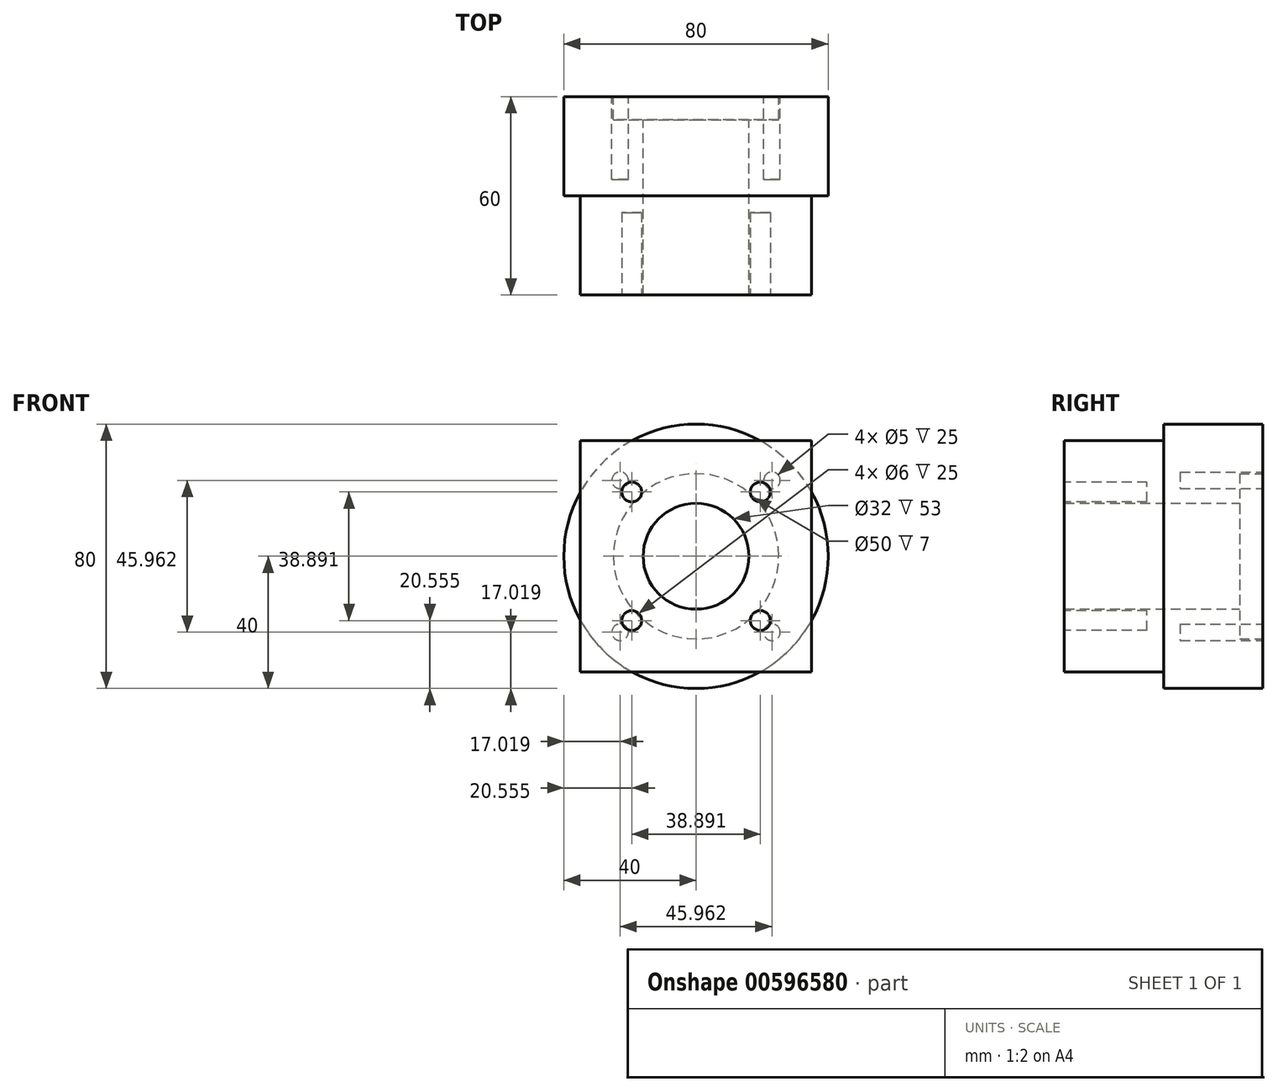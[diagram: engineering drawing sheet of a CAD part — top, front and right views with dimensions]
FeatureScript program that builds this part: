
annotation { "Feature Type Name" : "Feature", "Feature Type Description" : "" }
export const myFeature = defineFeature(function(context is Context, id is Id, definition is map)
    precondition{}
    {
        {
            var Q0;
            Q0=qCreatedBy(makeId("Front.planeOp"),FACE);
            var sketch = newSketch(context, id + "F0", { "sketchPlane" : qUnion([Q0])});
            skCircle(sketch, "E0", {"center": v(0, 0) * mm, "radius": 40 * mm});
            skSolve(sketch);
        }
        {
            var Q0;
            Q0=qSketchRegion(id+"F0",true);
            extrude(context, id + "F1", {"entities" : qUnion([Q0]), "depth" : 30 * mm, "offsetDistance" : 25 * mm});
        }
        {
            var Q0;
            Q0=makeQuery(id+"F1.opExtrude","CAP_FACE",FACE,{"disambiguationData":[OSD([sQuery(id+"F0.wireOp",EDGE,"E0")])],"isStart":false});
            var sketch = newSketch(context, id + "F2", { "sketchPlane" : qUnion([Q0])});
            skLineSegment(sketch, "E1.bottom", {"start": v(-35, -35) * mm, "end": v(35, -35) * mm});
            skLineSegment(sketch, "E1.top", {"start": v(-35, 35) * mm, "end": v(35, 35) * mm});
            skLineSegment(sketch, "E1.left", {"start": v(-35, -35) * mm, "end": v(-35, 35) * mm});
            skLineSegment(sketch, "E1.right", {"start": v(35, -35) * mm, "end": v(35, 35) * mm});
            skSolve(sketch);
        }
        {
            var Q0;
            Q0=qSketchRegion(id+"F2",true);
            extrude(context, id + "F3", {"entities" : qUnion([Q0]), "operationType" : NewBodyOperationType.ADD, "depth" : 30 * mm, "offsetDistance" : 25 * mm});
        }
        {
            var Q0;
            Q0=makeQuery(id+"F1.opExtrude","CAP_FACE",FACE,{"disambiguationData":[OSD([sQuery(id+"F0.wireOp",EDGE,"E0")])],"isStart":true});
            var sketch = newSketch(context, id + "F4", { "sketchPlane" : qUnion([Q0])});
            skCircle(sketch, "E2", {"center": v(0, 0) * mm, "radius": 16 * mm});
            skSolve(sketch);
        }
        {
            var Q0;
            Q0=makeQuery(id+"F4.imprint","IMPRINT",FACE,{"disambiguationData":[TD([[makeQuery(id+"F4.imprint","IMPRINT",EDGE,{"derivedFrom":sQuery(id+"F4.wireOp",EDGE,"E2")}),1.0]])]});
            extrude(context, id + "F5", {"entities" : qUnion([Q0]), "operationType" : NewBodyOperationType.REMOVE, "endBound" : BoundingType.THROUGH_ALL, "oppositeDirection" : true, "depth" : 25 * mm, "offsetDistance" : 25 * mm});
        }
        {
            var Q0;
            Q0=makeQuery(id+"F1.opExtrude","CAP_FACE",FACE,{"disambiguationData":[OSD([sQuery(id+"F0.wireOp",EDGE,"E0")])],"isStart":true});
            var sketch = newSketch(context, id + "F6", { "sketchPlane" : qUnion([Q0])});
            skCircle(sketch, "E3", {"center": v(0, 0) * mm, "radius": 25 * mm});
            skSolve(sketch);
        }
        {
            var Q0;
            Q0=makeQuery(id+"F6.imprint","IMPRINT",FACE,{"disambiguationData":[TD([[makeQuery(id+"F6.imprint","IMPRINT",EDGE,{"derivedFrom":sQuery(id+"F6.wireOp",EDGE,"E3")}),1.0]])]});
            extrude(context, id + "F7", {"entities" : qUnion([Q0]), "operationType" : NewBodyOperationType.REMOVE, "oppositeDirection" : true, "depth" : 7 * mm, "offsetDistance" : 25 * mm});
        }
        {
            var Q0;
            Q0=makeQuery(id+"F1.opExtrude","CAP_FACE",FACE,{"disambiguationData":[OSD([sQuery(id+"F0.wireOp",EDGE,"E0")])],"isStart":true});
            var sketch = newSketch(context, id + "F8", { "sketchPlane" : qUnion([Q0])});
            skCircle(sketch, "E4", {"center": v(0, 0) * mm, "radius": 32.5 * mm, "construction": true});
            skLineSegment(sketch, "E5", {"start": v(0, 0) * mm, "end": v(-22.98, 22.98) * mm, "construction": true});
            skCircle(sketch, "E6", {"center": v(-22.98, 22.98) * mm, "radius": 2.5 * mm});
            skCircle(sketch, "E7.1.0", {"center": v(-22.98, -22.98) * mm, "radius": 2.5 * mm});
            skCircle(sketch, "E7.2.0", {"center": v(22.98, -22.98) * mm, "radius": 2.5 * mm});
            skCircle(sketch, "E7.3.0", {"center": v(22.98, 22.98) * mm, "radius": 2.5 * mm});
            skSolve(sketch);
        }
        {
            var Q0;
            Q0=makeQuery(id+"F8.imprint","IMPRINT",FACE,{"disambiguationData":[TD([[makeQuery(id+"F8.imprint","IMPRINT",EDGE,{"derivedFrom":sQuery(id+"F8.wireOp",EDGE,"E6")}),1.0]])]});
            var Q1;
            Q1=makeQuery(id+"F8.imprint","IMPRINT",FACE,{"disambiguationData":[TD([[makeQuery(id+"F8.imprint","IMPRINT",EDGE,{"derivedFrom":sQuery(id+"F8.wireOp",EDGE,"E7.3.0")}),1.0]])]});
            var Q2;
            Q2=makeQuery(id+"F8.imprint","IMPRINT",FACE,{"disambiguationData":[TD([[makeQuery(id+"F8.imprint","IMPRINT",EDGE,{"derivedFrom":sQuery(id+"F8.wireOp",EDGE,"E7.2.0")}),1.0]])]});
            var Q3;
            Q3=makeQuery(id+"F8.imprint","IMPRINT",FACE,{"disambiguationData":[TD([[makeQuery(id+"F8.imprint","IMPRINT",EDGE,{"derivedFrom":sQuery(id+"F8.wireOp",EDGE,"E7.1.0")}),1.0]])]});
            extrude(context, id + "F9", {"entities" : qUnion([Q0, Q1, Q2, Q3]), "operationType" : NewBodyOperationType.REMOVE, "oppositeDirection" : true, "depth" : 25 * mm, "offsetDistance" : 25 * mm});
        }
        {
            var Q0;
            Q0=makeQuery(id+"F3.opExtrude","CAP_FACE",FACE,{"disambiguationData":[OSD([sQuery(id+"F2.wireOp",EDGE,"E1.bottom"),sQuery(id+"F2.wireOp",EDGE,"E1.top"),sQuery(id+"F2.wireOp",EDGE,"E1.left"),sQuery(id+"F2.wireOp",EDGE,"E1.right")])],"isStart":false});
            var sketch = newSketch(context, id + "F10", { "sketchPlane" : qUnion([Q0])});
            skCircle(sketch, "E8", {"center": v(0, 0) * mm, "radius": 27.5 * mm, "construction": true});
            skLineSegment(sketch, "E9", {"start": v(0, 0) * mm, "end": v(-19.45, 19.45) * mm, "construction": true});
            skCircle(sketch, "E10", {"center": v(-19.45, 19.45) * mm, "radius": 3 * mm});
            skCircle(sketch, "E11.1.0", {"center": v(-19.45, -19.45) * mm, "radius": 3 * mm});
            skCircle(sketch, "E11.2.0", {"center": v(19.45, -19.45) * mm, "radius": 3 * mm});
            skCircle(sketch, "E11.3.0", {"center": v(19.45, 19.45) * mm, "radius": 3 * mm});
            skSolve(sketch);
        }
        {
            var Q0;
            Q0=makeQuery(id+"F10.imprint","IMPRINT",FACE,{"disambiguationData":[TD([[makeQuery(id+"F10.imprint","IMPRINT",EDGE,{"derivedFrom":sQuery(id+"F10.wireOp",EDGE,"E10")}),1.0]])]});
            var Q1;
            Q1=makeQuery(id+"F10.imprint","IMPRINT",FACE,{"disambiguationData":[TD([[makeQuery(id+"F10.imprint","IMPRINT",EDGE,{"derivedFrom":sQuery(id+"F10.wireOp",EDGE,"E11.3.0")}),1.0]])]});
            var Q2;
            Q2=makeQuery(id+"F10.imprint","IMPRINT",FACE,{"disambiguationData":[TD([[makeQuery(id+"F10.imprint","IMPRINT",EDGE,{"derivedFrom":sQuery(id+"F10.wireOp",EDGE,"E11.2.0")}),1.0]])]});
            var Q3;
            Q3=makeQuery(id+"F10.imprint","IMPRINT",FACE,{"disambiguationData":[TD([[makeQuery(id+"F10.imprint","IMPRINT",EDGE,{"derivedFrom":sQuery(id+"F10.wireOp",EDGE,"E11.1.0")}),1.0]])]});
            extrude(context, id + "F11", {"entities" : qUnion([Q0, Q1, Q2, Q3]), "operationType" : NewBodyOperationType.REMOVE, "oppositeDirection" : true, "depth" : 25 * mm, "offsetDistance" : 25 * mm});
        }
    });
